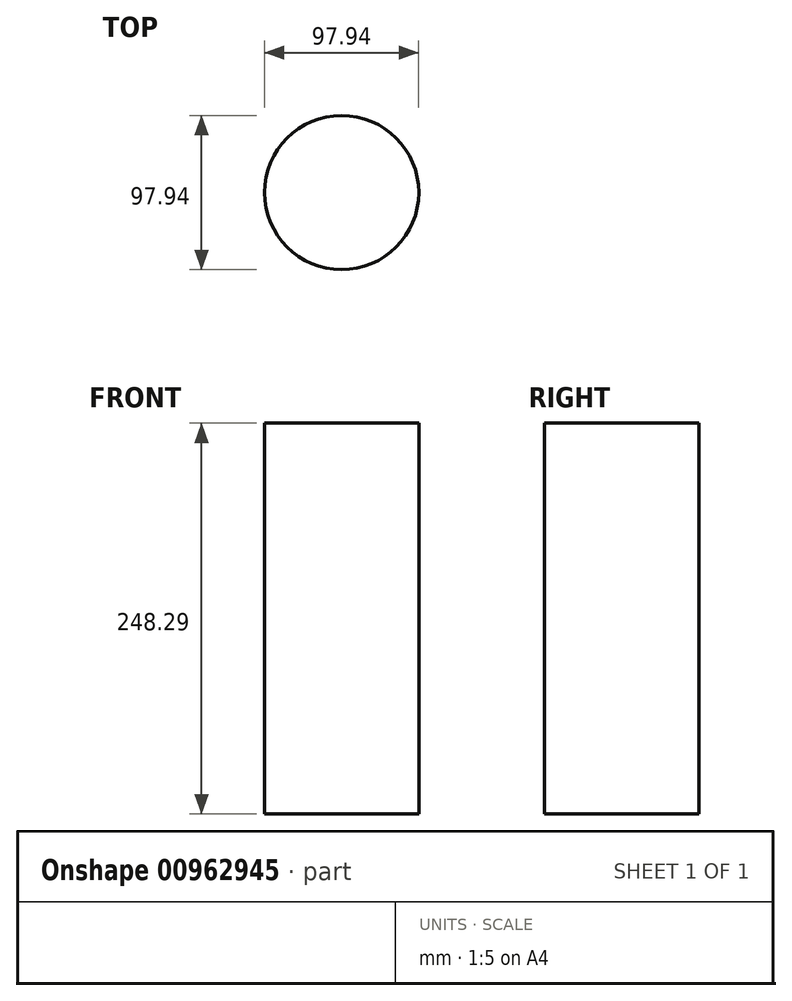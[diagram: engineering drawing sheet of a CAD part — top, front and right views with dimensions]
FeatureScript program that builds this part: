
annotation { "Feature Type Name" : "Feature", "Feature Type Description" : "" }
export const myFeature = defineFeature(function(context is Context, id is Id, definition is map)
    precondition{}
    {
        {
            var Q0;
            Q0=qCreatedBy(makeId("Top.planeOp"),FACE);
            var sketch = newSketch(context, id + "F0", { "sketchPlane" : qUnion([Q0])});
            skCircle(sketch, "E0", {"center": v(0, 0) * mm, "radius": 48.97 * mm});
            skSolve(sketch);
        }
        {
            var Q0;
            Q0=makeQuery(id+"F0.imprint","IMPRINT",FACE,{"disambiguationData":[TD([[makeQuery(id+"F0.imprint","IMPRINT",EDGE,{"derivedFrom":sQuery(id+"F0.wireOp",EDGE,"E0")}),1.0]])]});
            extrude(context, id + "F1", {"entities" : qUnion([Q0]), "depth" : 248.3 * mm, "offsetDistance" : 25.4 * mm});
        }
    });
